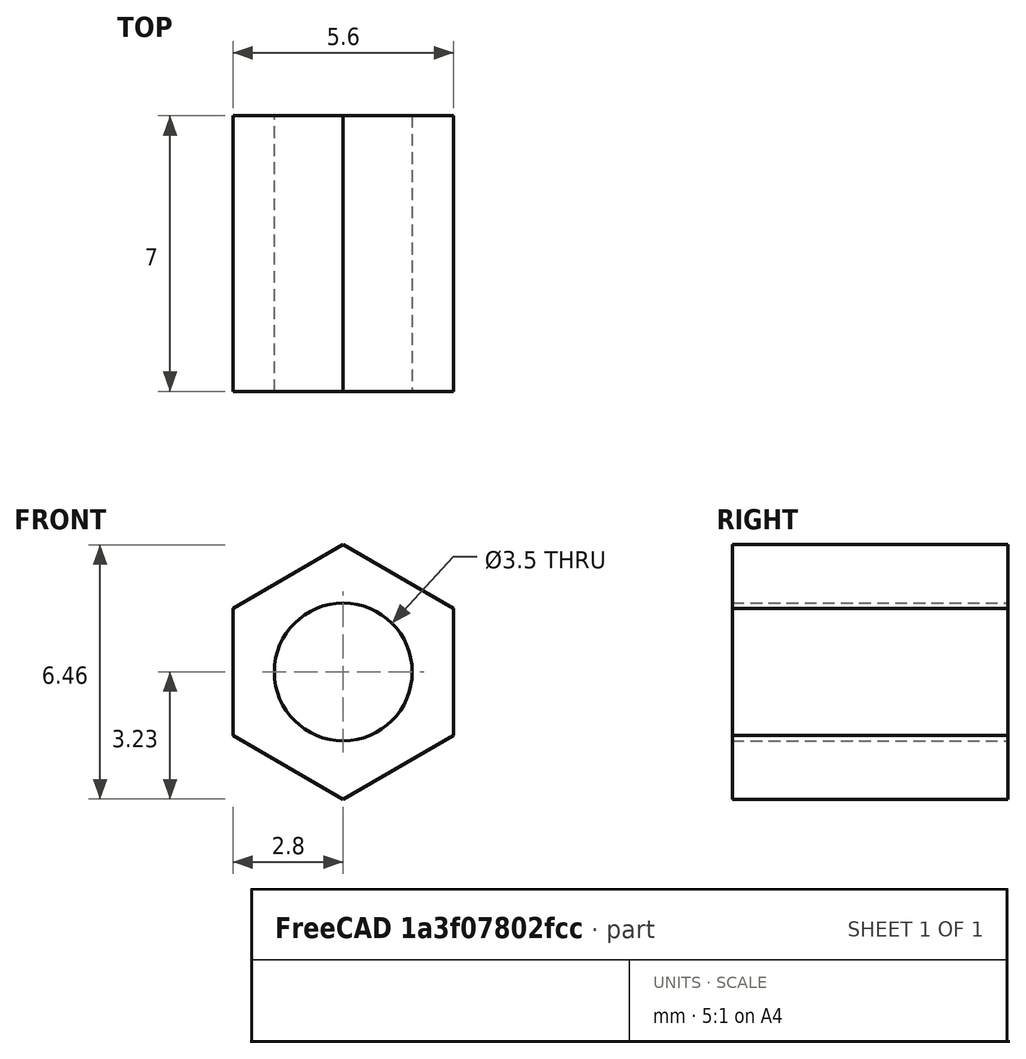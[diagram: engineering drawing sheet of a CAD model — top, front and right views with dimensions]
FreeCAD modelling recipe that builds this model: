
FCSTD DOCUMENT  (FreeCAD 2023.521R14555 (Git shallow))
Label: NutHolder
License: All rights reserved
objects: Sketcher::SketchObject×1, PartDesign::Pad×1, PartDesign::Body×1
note: 6 computed .brp shape members not serialized (recipe doc carries the construction recipe); baked Part::Feature solids carry a one-line shape summary decoded from their .brp

FEATURE [Sketcher::SketchObject] Sketch
  ArcFitTolerance = 1e-06
  AttachmentSupport = -> [XZ_Plane]
  ExternalBSplineMaxDegree = 5
  ExternalBSplineTolerance = 0.0001
  FullyConstrained = true
  InternalTolerance = 1e-06
  InvalidShape = false
  MakeInternals = false
  MapMode = 5
  Placement = pos=(0,0,0) rot=(1,0,0;1.5708rad)
  Support = -> [XZ_Plane]
  TreeRank = 11
  ValidateShape = false
  sketch-geometry (8):
    g0: LineSegment StartX=2.8 StartY=1.61658 StartZ=0 EndX=0 EndY=3.23316 EndZ=0
    g1: LineSegment StartX=0 StartY=3.23316 StartZ=0 EndX=-2.8 EndY=1.61658 EndZ=0
    g2: LineSegment StartX=-2.8 StartY=1.61658 StartZ=0 EndX=-2.8 EndY=-1.61658 EndZ=0
    g3: LineSegment StartX=-2.8 StartY=-1.61658 StartZ=0 EndX=0 EndY=-3.23316 EndZ=0
    g4: LineSegment StartX=0 StartY=-3.23316 StartZ=0 EndX=2.8 EndY=-1.61658 EndZ=0
    g5: LineSegment StartX=2.8 StartY=-1.61658 StartZ=0 EndX=2.8 EndY=1.61658 EndZ=0
    g6: Circle [constr] CenterX=0 CenterY=0 CenterZ=0 NormalX=0 NormalY=0 NormalZ=1 AngleXU=0 Radius=3.23316
    g7: Circle CenterX=0 CenterY=0 CenterZ=0 NormalX=0 NormalY=0 NormalZ=1 AngleXU=0 Radius=1.75
  constraints (18):
    c: Coincident(g0,g1)
    c: Coincident(g1,g2)
    c: Coincident(g2,g3)
    c: Coincident(g3,g4)
    c: Coincident(g4,g5)
    c: Coincident(g5,g0)
    c: Equal(g0, g1-g5) x5
    c: PointOnObject(g0,g6)
    c: PointOnObject(g1,g6)
    c: PointOnObject(g2,g6)
    c: PointOnObject(g3,g6)
    c: PointOnObject(g4,g6)
    c: PointOnObject(g5,g6)
    c: Coincident(g6,g-1)
    c: Vertical(g0,g6)
    c: DistanceX(g1,g0) = 5.6
    c: Coincident(g7,g6)
    c: Diameter(g7) = 3.5
FEATURE [PartDesign::Pad] Pad
  AddSubType = 0
  AlongSketchNormal = false
  AutoTaperInnerAngle = true
  CheckUpToFaceLimits = true
  ClaimChildren = false
  Direction = (0,-1,2e-16)
  Fit = 0
  FitJoin = 0
  InnerFit = 0
  InnerFitJoin = 0
  InvalidShape = false
  Length = 7
  Length2 = 10
  Linearize = true
  NewSolid = false
  Profile = -> Sketch
  ReferenceAxis = -> Sketch [N_Axis]
  Suppress = false
  TaperInnerAngle = 0
  TaperInnerAngleRev = 0
  TreeRank = 12
  Type = 0
  ValidateShape = true
  _ProfileBasedVersion = 1
FEATURE [PartDesign::Body] Body
  AutoGroupSolids = false
  ClaimAllChildren = false
  ExportMode = 0
  Group = -> [Sketch,Pad]
  InvalidShape = false
  Origin = -> Origin
  Tip = -> Pad
  TreeRank = 10
  ValidateShape = false
  _ExportChildren = -> [Pad]
  _GroupVersion = 1
